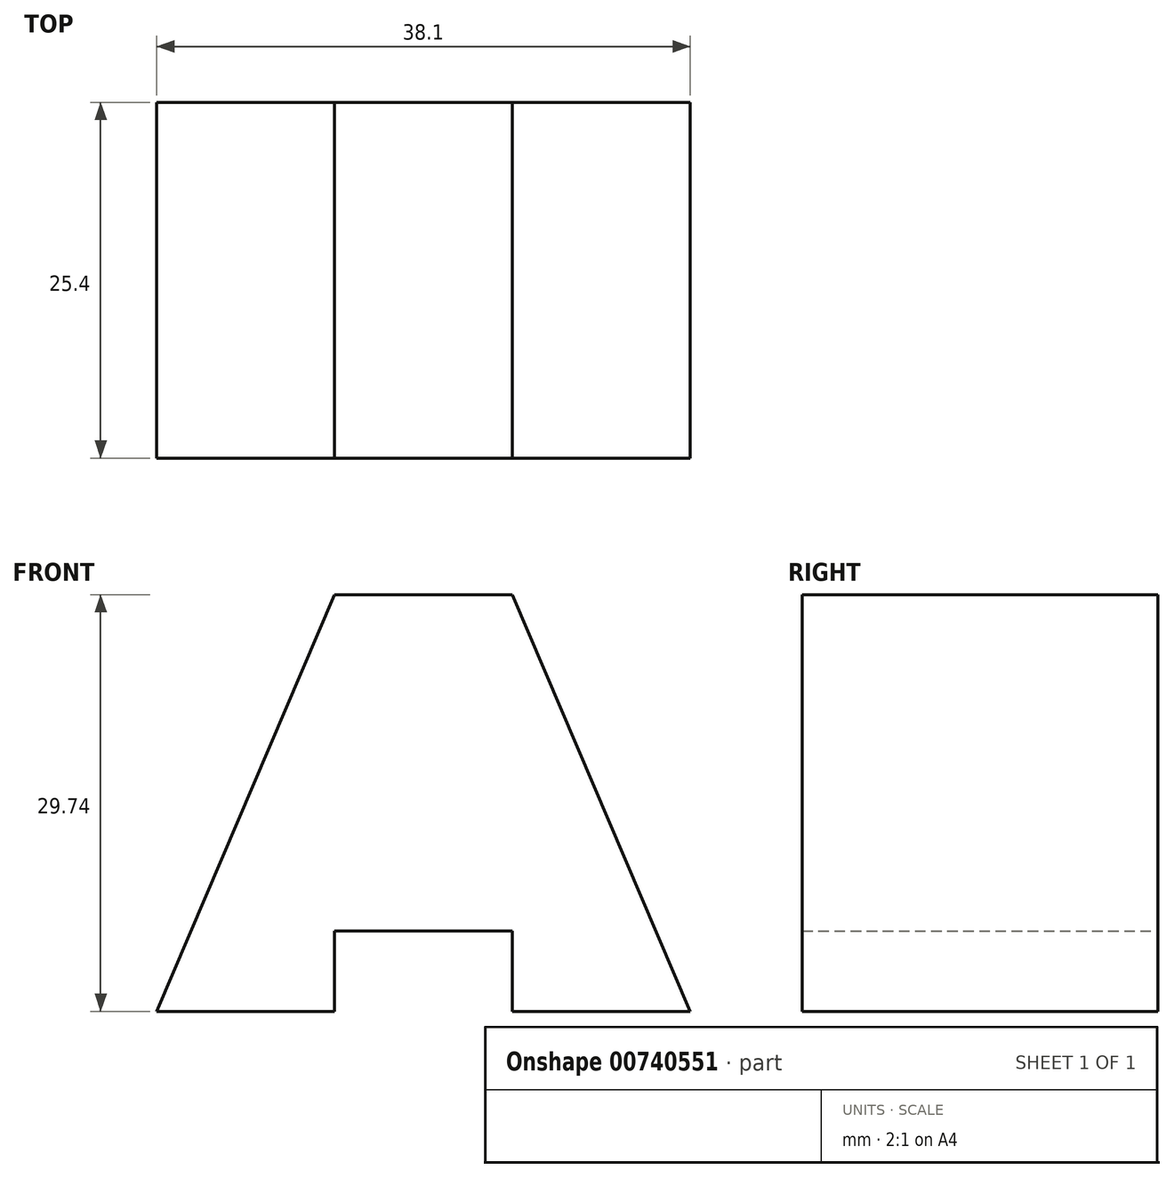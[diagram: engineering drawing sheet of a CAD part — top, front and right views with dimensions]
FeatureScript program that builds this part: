
annotation { "Feature Type Name" : "Feature", "Feature Type Description" : "" }
export const myFeature = defineFeature(function(context is Context, id is Id, definition is map)
    precondition{}
    {
        {
            var Q0;
            Q0=qCreatedBy(makeId("Front.planeOp"),FACE);
            var sketch = newSketch(context, id + "F0", { "sketchPlane" : qUnion([Q0])});
            skLineSegment(sketch, "E0", {"start": v(0, 0) * mm, "end": v(12.7, 29.74) * mm});
            skLineSegment(sketch, "E1", {"start": v(12.7, 29.74) * mm, "end": v(25.4, 29.74) * mm});
            skLineSegment(sketch, "E2", {"start": v(25.4, 29.74) * mm, "end": v(38.1, 0) * mm});
            skLineSegment(sketch, "E3", {"start": v(38.1, 0) * mm, "end": v(25.4, 0) * mm});
            skLineSegment(sketch, "E4", {"start": v(25.4, 0) * mm, "end": v(25.4, 5.72) * mm});
            skLineSegment(sketch, "E5", {"start": v(25.4, 5.72) * mm, "end": v(12.7, 5.72) * mm});
            skLineSegment(sketch, "E6", {"start": v(12.7, 5.72) * mm, "end": v(12.7, 0) * mm});
            skLineSegment(sketch, "E7", {"start": v(12.7, 0) * mm, "end": v(0, 0) * mm});
            skSolve(sketch);
        }
        {
            var Q0;
            Q0=makeQuery(id+"F0.imprint","IMPRINT",FACE,{"disambiguationData":[TD([[makeQuery(id+"F0.imprint","IMPRINT",EDGE,{"derivedFrom":sQuery(id+"F0.wireOp",EDGE,"E0")}),-1.0]])]});
            extrude(context, id + "F1", {"entities" : qUnion([Q0]), "depth" : 25.4 * mm, "offsetDistance" : 25.4 * mm});
        }
    });
